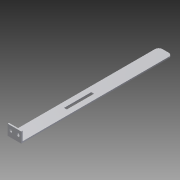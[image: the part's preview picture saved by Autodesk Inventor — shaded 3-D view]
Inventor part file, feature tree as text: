
AUTODESK INVENTOR PART (.ipt)
format: ipt  version: 2015 (Build 190159000, 159)  size: 127,488 bytes
history: native  units: mm
features: sketch x4, extrude x3, other x1, hole x1, fillet x1
ambient origin geometry x8: Origin, YZ Plane, XZ Plane, XY Plane, X Axis, Y Axis, Z Axis, Center Point
bodies: Body1 (feature_tree)
feature tree (10):
  other  "ソリッド1"
  extrude  "押し出し1"  Depth=15.0mm
  extrude  "押し出し2"  Depth=166.0mm
  extrude  "押し出し3"  Depth=1.5mm TaperAngle=0.0deg
  hole  "穴1"  [1 undecoded]
  fillet  "フィレット1"  Radius=30.0mm
  sketch  "スケッチ1"
  sketch  "スケッチ2"
  sketch  "スケッチ3"
  sketch  "スケッチ4"
note: 1 required parameter value undecoded (feature->parameter linkage not recoverable at this tier; creation-order binding heuristic only, values carry confidence <= 0.55)
